# Revit family: KR4050001_Teleducha_Koral
name_source: partatom
category: Plumbing Fixtures
units: mm (PartAtom-declared; Revit-internal decimal feet)

## family parameters
Always vertical = Yes
Cut with Voids When Loaded = No
OmniClass Number = 23.31.11.00
OmniClass Title = Faucets
Part Type = Normal
Room Calculation Point = No
Round Connector Dimension = Use Diameter
Shared = No
Work Plane-Based = No

## types (1)
- KR4050001_Teleducha_Koral
    Capacidad de flujo = máximo a 80 psi: 9,3 L/min.
    Creado por = BIMBAU
    Default Elevation = 0 mm  [stored 0 ft]
    Description = Con la teleducha Koral disfrutarás de la sistema MultiFlow que ofrece mayor relajación gracias a sus diferentes tipos de chorro.
    Fecha de creación = 09/04/2021
    Garantía = 30 años
    Garantía Acabados = 2 años
    Manufacturer = Corona
    Material = Corona_Acero inoxidable
    Material 2 = Corona_Plastico_Gris
    Model = Teleducha Koral
    Peso neto = 432 g. - 0,9 lb.
    Presion maxima = 125 psi (860 kPa).
    Presion minima = 20 psi (140 kPa).
    Referencia = KR4050001
    Resistencia = Resistente a la corrosión, pelado y decoloración por agua
    Temperatura de uso = 5˚C a 71˚C.
    URL = https://corona.co

note: [stored X ft] marks values corroborated as IEEE doubles in the binary element streams (Revit-internal decimal feet)

## geometry (parser evidence)
native form markers: Sweep x4
no freeform markers — native parametric forms only
